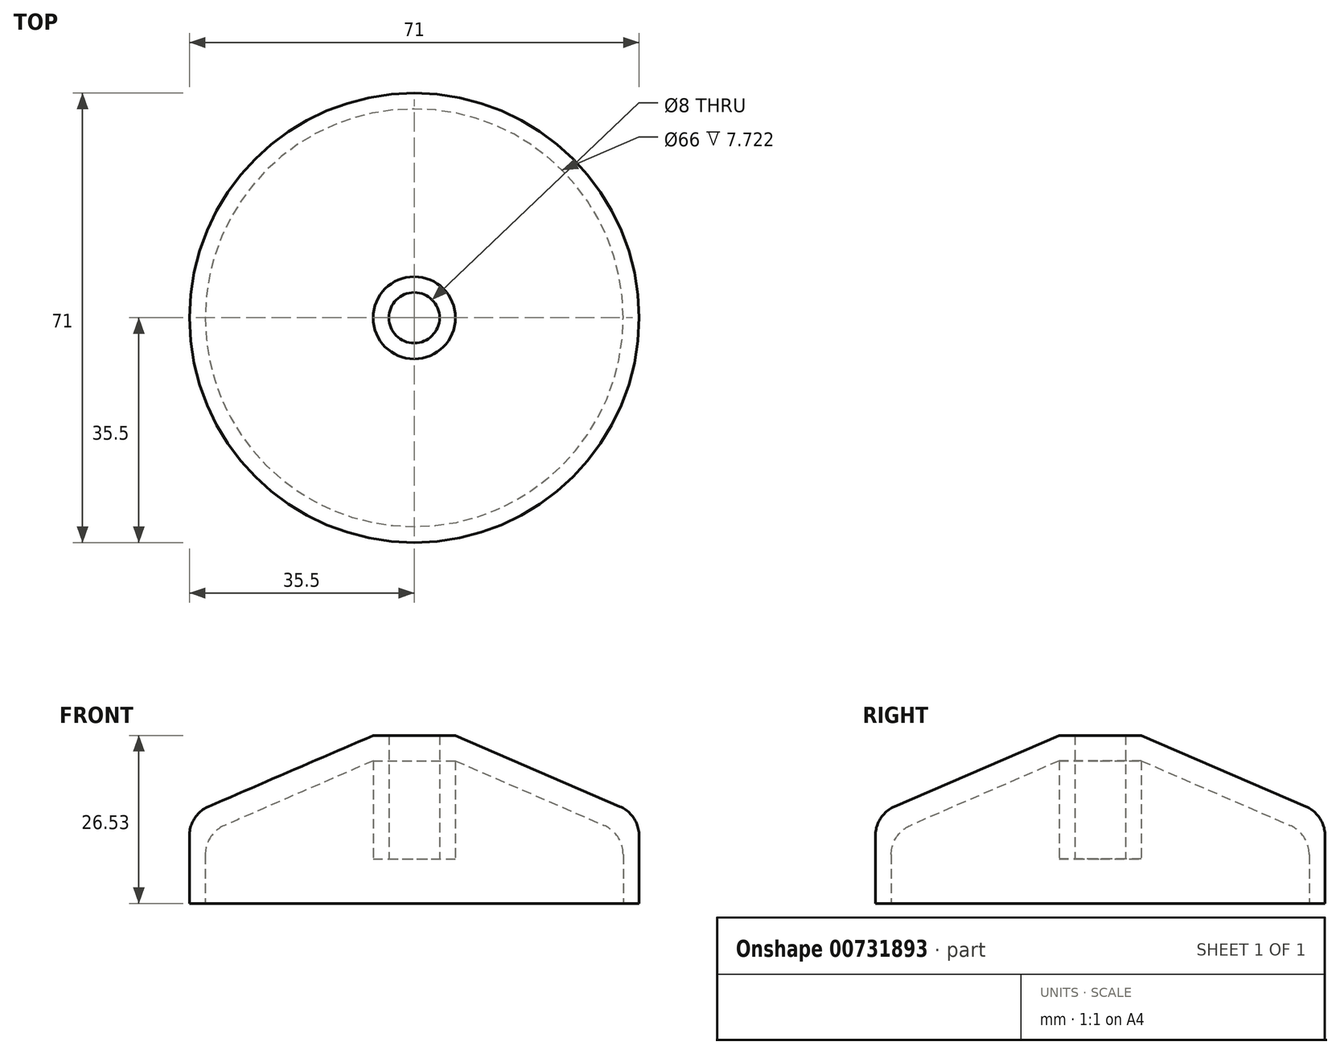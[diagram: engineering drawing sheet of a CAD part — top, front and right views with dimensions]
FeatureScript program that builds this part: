
annotation { "Feature Type Name" : "Feature", "Feature Type Description" : "" }
export const myFeature = defineFeature(function(context is Context, id is Id, definition is map)
    precondition{}
    {
        {
            var Q0;
            Q0=qCreatedBy(makeId("Front.planeOp"),FACE);
            var sketch = newSketch(context, id + "F0", { "sketchPlane" : qUnion([Q0])});
            skLineSegment(sketch, "E0", {"start": v(0, 0) * mm, "end": v(0, 69.24) * mm, "construction": true});
            skLineSegment(sketch, "E1", {"start": v(0, 0) * mm, "end": v(33, 0) * mm, "construction": true});
            skLineSegment(sketch, "E2", {"start": v(33, 0) * mm, "end": v(33, -11) * mm});
            skLineSegment(sketch, "E3", {"start": v(33, -11) * mm, "end": v(35.5, -11) * mm});
            skLineSegment(sketch, "E4", {"start": v(35.5, -11) * mm, "end": v(35.5, 3) * mm});
            skLineSegment(sketch, "E5", {"start": v(0, 0) * mm, "end": v(4, 0) * mm, "construction": true});
            skLineSegment(sketch, "E6", {"start": v(4, 44.49) * mm, "end": v(4, 0) * mm, "construction": true});
            skLineSegment(sketch, "E7", {"start": v(4, 15.53) * mm, "end": v(4, -4) * mm});
            skLineSegment(sketch, "E8", {"start": v(4, -4) * mm, "end": v(6.5, -4) * mm});
            skLineSegment(sketch, "E9", {"start": v(6.5, -4) * mm, "end": v(6.5, 11.53) * mm});
            skLineSegment(sketch, "E10", {"start": v(33, 0) * mm, "end": v(6.5, 11.53) * mm});
            skLineSegment(sketch, "E11", {"start": v(4, 15.53) * mm, "end": v(6.5, 15.53) * mm});
            skLineSegment(sketch, "E12", {"start": v(6.5, 15.53) * mm, "end": v(35.5, 3) * mm});
            skSolve(sketch);
        }
        {
            var Q0;
            Q0=makeQuery(id+"F0.imprint","IMPRINT",FACE,{"disambiguationData":[TD([[makeQuery(id+"F0.imprint","IMPRINT",EDGE,{"derivedFrom":sQuery(id+"F0.wireOp",EDGE,"E2")}),1.0]])]});
            var Q1;
            Q1=sQuery(id+"F0.wireOp",EDGE,"E0");
            revolve(context, id + "F1", {"surfaceOperationType" : NewSurfaceOperationType.NEW, "entities" : qUnion([Q0]), "axis" : qUnion([Q1]), "revolveType" : RevolveType.FULL});
        }
        {
            var Q0;
            Q0=makeQuery(id+"F1.opRevolve","SWEPT_EDGE",EDGE,{"disambiguationData":[OSD([sQuery(id+"F0.wireOp",EDGE,"E4"),sQuery(id+"F0.wireOp",EDGE,"E12")])]});
            var Q1;
            Q1=makeQuery(id+"F1.opRevolve","SWEPT_EDGE",EDGE,{"disambiguationData":[OSD([sQuery(id+"F0.wireOp",EDGE,"E2"),sQuery(id+"F0.wireOp",EDGE,"E10")])]});
            fillet(context, id + "F2", {"entities" : qUnion([Q0, Q1]), "radius" : 5 * mm, "tangentPropagation" : true, "allowEdgeOverflow" : false});
        }
    });
